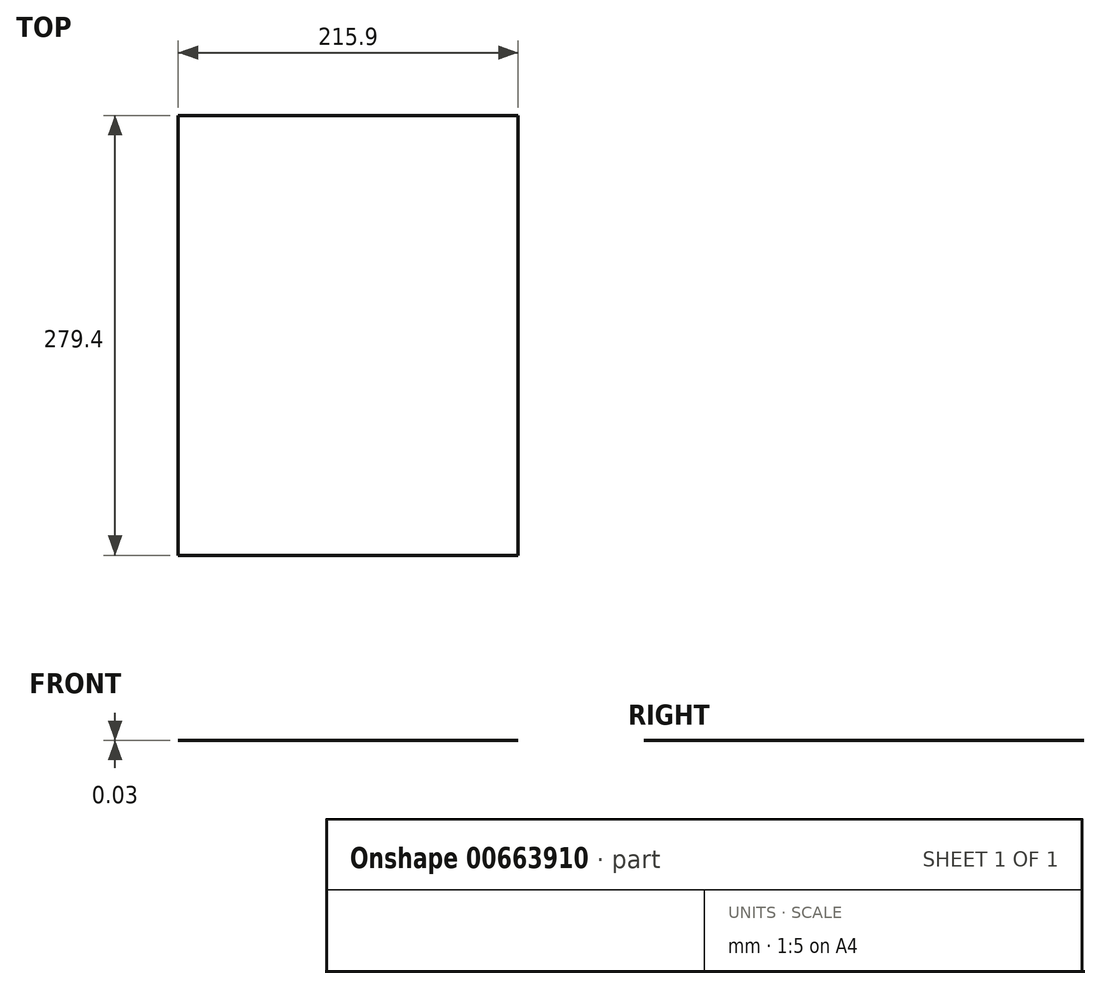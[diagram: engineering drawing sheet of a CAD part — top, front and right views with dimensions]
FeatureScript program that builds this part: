
annotation { "Feature Type Name" : "Feature", "Feature Type Description" : "" }
export const myFeature = defineFeature(function(context is Context, id is Id, definition is map)
    precondition{}
    {
        {
            var Q0;
            Q0=qCreatedBy(makeId("Top.planeOp"),FACE);
            var sketch = newSketch(context, id + "F0", { "sketchPlane" : qUnion([Q0])});
            skLineSegment(sketch, "E0.bottom", {"start": v(-105.87, 168.05) * mm, "end": v(110.03, 168.05) * mm});
            skLineSegment(sketch, "E0.top", {"start": v(-105.87, -111.35) * mm, "end": v(110.03, -111.35) * mm});
            skLineSegment(sketch, "E0.left", {"start": v(-105.87, 168.05) * mm, "end": v(-105.87, -111.35) * mm});
            skLineSegment(sketch, "E0.right", {"start": v(110.03, 168.05) * mm, "end": v(110.03, -111.35) * mm});
            skSolve(sketch);
        }
        {
            var Q0;
            Q0=makeQuery(id+"F0.imprint","IMPRINT",FACE,{"disambiguationData":[TD([[makeQuery(id+"F0.imprint","IMPRINT",EDGE,{"derivedFrom":sQuery(id+"F0.wireOp",EDGE,"E0.bottom")}),-1.0]])]});
            extrude(context, id + "F1", {"entities" : qUnion([Q0]), "depth" : 0.03 * mm, "offsetDistance" : 25.4 * mm});
        }
    });
